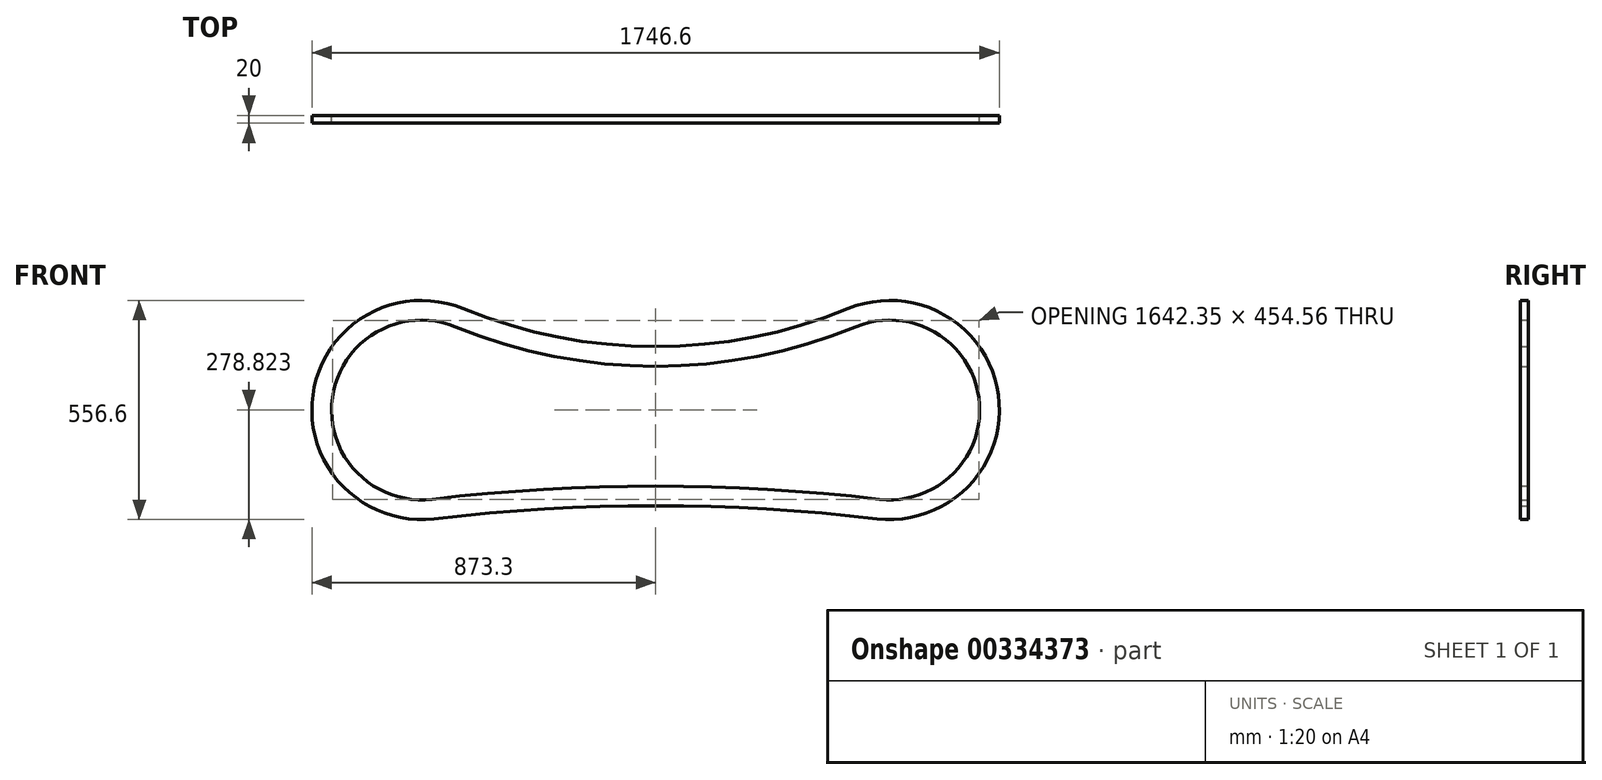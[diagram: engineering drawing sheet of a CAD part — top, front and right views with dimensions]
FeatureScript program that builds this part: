
annotation { "Feature Type Name" : "Feature", "Feature Type Description" : "" }
export const myFeature = defineFeature(function(context is Context, id is Id, definition is map)
    precondition{}
    {
        {
            var Q0;
            Q0=qCreatedBy(makeId("Front.planeOp"),FACE);
            var sketch = newSketch(context, id + "F0", { "sketchPlane" : qUnion([Q0])});
            skArc(sketch, "E0", {"start": v(-489.57, 244.9) * mm, "mid": v(-870.96, 25.35) * mm, "end": v(-562.96, -288.98) * mm});
            skArc(sketch, "E1", {"start": v(562.46, -288.98) * mm, "mid": v(870.46, 25.35) * mm, "end": v(489.07, 244.9) * mm});
            skArc(sketch, "E2", {"start": v(562.46, -288.98) * mm, "mid": v(-0.25, -256.22) * mm, "end": v(-562.96, -288.98) * mm});
            skPoint(sketch, "E2.centerSnap0", {"position": v(-0.25, -12.56) * mm});
            skArc(sketch, "E3", {"start": v(-489.57, 244.9) * mm, "mid": v(-0.25, 148.37) * mm, "end": v(489.07, 244.9) * mm});
            skArc(sketch, "E4.0", {"start": v(-508.55, 198.64) * mm, "mid": v(-821.42, 18.54) * mm, "end": v(-568.76, -239.31) * mm});
            skArc(sketch, "E4.1", {"start": v(-508.55, 198.64) * mm, "mid": v(-0.25, 98.37) * mm, "end": v(508.05, 198.64) * mm});
            skArc(sketch, "E4.2", {"start": v(568.26, -239.31) * mm, "mid": v(820.92, 18.54) * mm, "end": v(508.05, 198.64) * mm});
            skArc(sketch, "E4.3", {"start": v(568.26, -239.31) * mm, "mid": v(-0.25, -206.22) * mm, "end": v(-568.76, -239.31) * mm});
            skSolve(sketch);
        }
        {
            var Q0;
            Q0=makeQuery(id+"F0.imprint","IMPRINT",FACE,{"disambiguationData":[TD([[makeQuery(id+"F0.imprint","IMPRINT",EDGE,{"derivedFrom":sQuery(id+"F0.wireOp",EDGE,"E0")}),1.0]])]});
            extrude(context, id + "F1", {"entities" : qUnion([Q0]), "depth" : 20 * mm});
        }
    });
